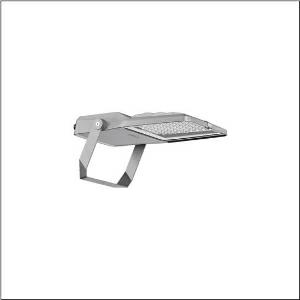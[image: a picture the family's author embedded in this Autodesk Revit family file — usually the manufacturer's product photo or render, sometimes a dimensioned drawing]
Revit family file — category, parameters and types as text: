
# Revit family: floodlight_fl_21_mini___pl64_5xa7776b4e1a_9990
name_source: partatom
category: Lighting Fixtures
units: mm (PartAtom-declared; Revit-internal decimal feet)

## family parameters
Cut with Voids When Loaded = No
Host = Face
Light Source = No
Part Type = Normal
Room Calculation Point = No
Round Connector Dimension = Use Diameter
Shared = No

## types (1)
- --- (1 x LED, 6260 lm, 45.7 W, 4000K)
    Apparent Load = 46 VA
    CIE Flux Codes = 28 80 98 100 100
    Color Rendering = 70
    Color Temperature = 4000K
    Default Elevation = 1800 mm
    Description = Floodlight FL 21 mini, floodlight, primary light control with lens, of PMMA, primary optical cover: protective disc, of toughened safety glass, transparent, light distribution: PL64, light emission: direct distribution, installation type: surface-mounted, LED, High Power LED, rated luminous flux: 6.260lm, luminous efficacy: 137lm/W, light colour: 740, colour temperature: 4000K, control gear: D4iSmart Interface (Zhaga), control: overheat protection, constant luminous flux control, time-dependent luminous flux control, flexible luminous flux parameterisation, pre-setting: logarithmic dimming characteristic, with terminal, 6-pole, mains connection: 220..240V, AC, 50/60Hz, start of lifetime: 46W, end of service life: 48W, reduction: 22W, mounting bracket, of diecast aluminium, powder-coated, SITECO metallic grey (DB 702S), corrosivity category C5 mid according to DIN EN ISO 12944, suitable for swimming pools, chlorine-resistant, sealing non-destructively replaceable, mounting bracket, of steel, galvanised, powder-coated, SITECO metallic grey (DB 702S), Smart Interface below and above, protection rating (complete): IP66, insulation class (complete): insulation class II (safety insulation), certification: CE, ENEC, VDE, protection symbol: D, impact resistance: IK08, permissible operating ambient temperature: -40..+40°C, permissible operating ambient temperature for outdoor applications: -40..+50°C, standard: DIN EN 12944, LABS conformity tested according to VDMA 24364:2018-05, packaging unit: 1 piece

Light Distribution: PL64
    Height = 70 mm
    Lamp = 1 x LED
    Lamp Light Flux = 6260 lm
    Lamp Power = 45.7 W
    Lamp count = 1
    Length = 485 mm
    Luminous efficacy = 137 lm/W
    Manufacturer = Siteco
    ModVariant = No
    Model = 5XA7776B4E1A
    Number of Poles = 1
    OnlyDefault = Yes
    Power Factor = 1
    Product Name = Floodlight FL 21 mini | PL64
    Product group = floodlight | pylon annexe
    ProductGroupID = 6201
    Protection Class = Protection class II
    Protection Degree = IP 66
    RLX_Detail_Level = 1
    RLX_Emergency_Light_Flux = 0 lm
    RLX_Emergency_Type = 0
    RLX_Emergency_Type_DB = No
    RlxData = <blob elided: 96073 chars, md5=4154ff25>
    Socket = socket
    Standby Power = 0 W
    System Light Flux = 6260 lm
    System Power = 46 W
    Type Comments = factory setting: luminous flux: 100 % | dim-lin: 254 | 463 mA
    Type Image = l_1006845.jpg
    URL = http://relux.com
    VarID = @adj_100079
    Voltage = 0 V
    Weight = 0.00 kg
    Width = 337 mm

## geometry (parser evidence)
native form markers: Blend x4, Sweep x11
no freeform markers — native parametric forms only
